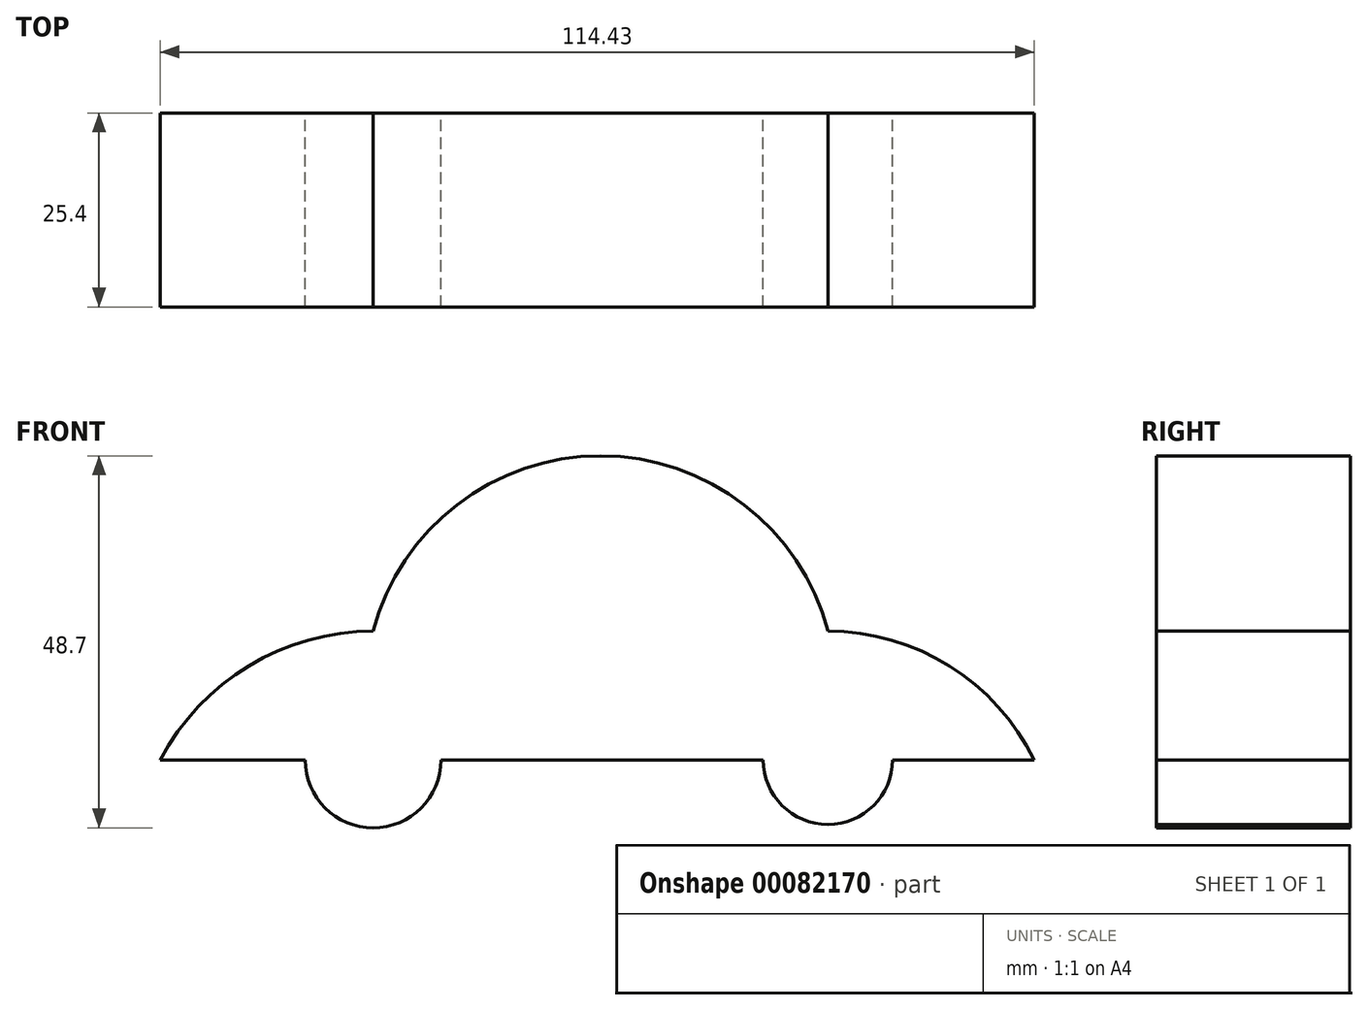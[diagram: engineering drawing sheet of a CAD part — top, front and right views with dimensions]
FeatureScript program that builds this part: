
annotation { "Feature Type Name" : "Feature", "Feature Type Description" : "" }
export const myFeature = defineFeature(function(context is Context, id is Id, definition is map)
    precondition{}
    {
        {
            var Q0;
            Q0=qCreatedBy(makeId("Front.planeOp"),FACE);
            var sketch = newSketch(context, id + "F0", { "sketchPlane" : qUnion([Q0])});
            skLineSegment(sketch, "E0.bottom", {"start": v(-38.34, 19.31) * mm, "end": v(21.2, 19.31) * mm});
            skLineSegment(sketch, "E0.top", {"start": v(-38.34, 2.47) * mm, "end": v(21.2, 2.47) * mm});
            skLineSegment(sketch, "E0.left", {"start": v(-38.34, 19.31) * mm, "end": v(-38.34, 2.47) * mm});
            skLineSegment(sketch, "E0.right", {"start": v(21.2, 19.31) * mm, "end": v(21.2, 2.47) * mm});
            skArc(sketch, "E1", {"start": v(-38.34, 19.31) * mm, "mid": v(-54.62, 14.77) * mm, "end": v(-66.22, 2.47) * mm});
            skArc(sketch, "E2", {"start": v(48.2, 2.47) * mm, "mid": v(37.12, 14.76) * mm, "end": v(21.2, 19.31) * mm});
            skLineSegment(sketch, "E3", {"start": v(-66.22, 2.47) * mm, "end": v(-38.34, 2.47) * mm});
            skLineSegment(sketch, "E4", {"start": v(21.2, 2.47) * mm, "end": v(48.2, 2.47) * mm});
            skArc(sketch, "E5", {"start": v(21.2, 19.31) * mm, "mid": v(-8.57, 42.28) * mm, "end": v(-38.34, 19.31) * mm});
            skCircle(sketch, "E6", {"center": v(-38.34, 2.47) * mm, "radius": 8.89 * mm});
            skCircle(sketch, "E7", {"center": v(21.2, 2.47) * mm, "radius": 8.47 * mm});
            skSolve(sketch);
        }
        {
            var Q0;
            Q0 = qSketchRegion(id + "F0", true);
            extrude(context, id + "F1", {"entities" : qUnion([Q0]), "depth" : 25.4 * mm});
        }
    });
